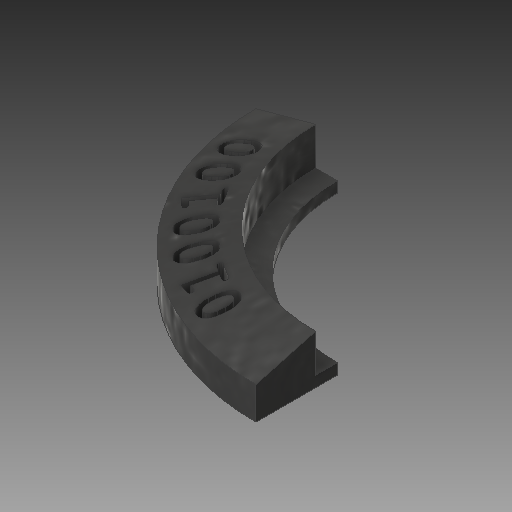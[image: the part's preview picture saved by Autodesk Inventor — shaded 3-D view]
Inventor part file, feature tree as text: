
AUTODESK INVENTOR PART (.ipt)
format: ipt  version: 2017 (Build 210142000, 142)  size: 441,344 bytes
history: native  units: in
note: dims shown in document units (in); Inventor stores cm internally (conversion verified against a paired STEP export)
features: sketch x3, extrude x2, revolve x1, projected_geometry x1
ambient origin geometry x8: Origin, YZ Plane, XZ Plane, XY Plane, X Axis, Y Axis, Z Axis, Center Point
bodies: Solid1 (feature_tree)
feature tree (7):
  revolve  "Revolution1"  [1 undecoded]
  extrude  "Extrusion1"  Depth=0.05in
  extrude  "Extrusion2"  Depth=0.275in
  sketch  "Sketch1"  dims[d0=0.8265in d1=0.175in]
  sketch  "Sketch2"  dims[d2=0.05in d3=0.1in]
  projected_geometry  "Projected Loop1"
  sketch  "Sketch3"  dims[d4=0.15in d5=0.275in d6=90.0deg d7=0.075in d8=1.0in d9=0.0in d10=1.0in d11=0.0in]
note: 1 required parameter value undecoded (feature->parameter linkage not recoverable at this tier; creation-order binding heuristic only, values carry confidence <= 0.55)
